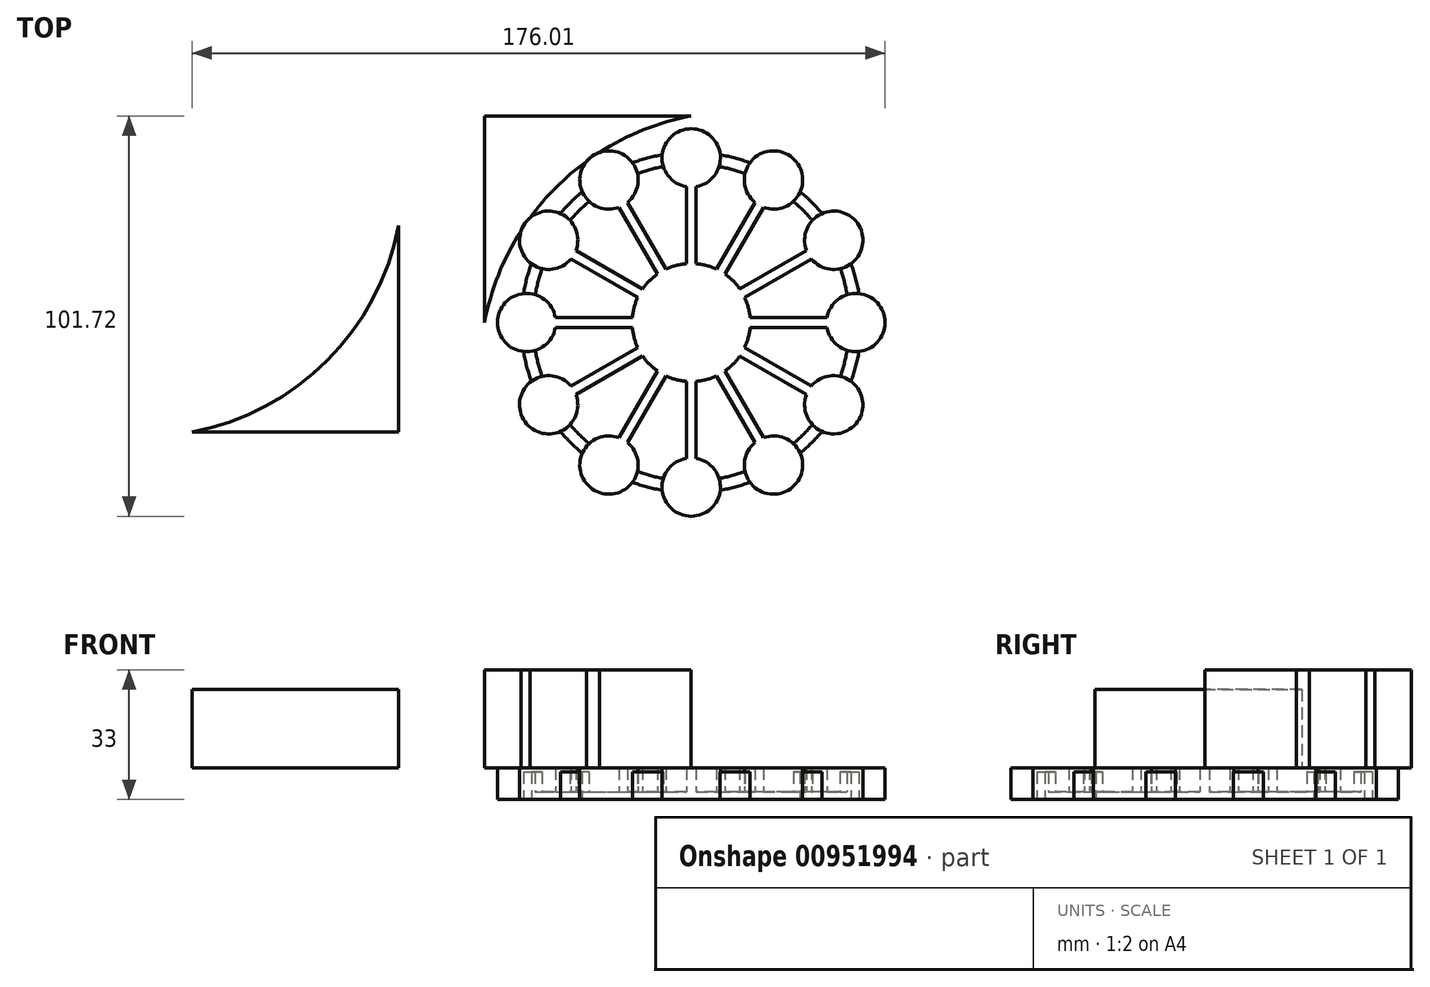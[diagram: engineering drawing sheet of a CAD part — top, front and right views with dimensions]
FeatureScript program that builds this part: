
annotation { "Feature Type Name" : "Feature", "Feature Type Description" : "" }
export const myFeature = defineFeature(function(context is Context, id is Id, definition is map)
    precondition{}
    {
        {
            var Q0;
            Q0=qCreatedBy(makeId("Top.planeOp"),FACE);
            var sketch = newSketch(context, id + "F0", { "sketchPlane" : qUnion([Q0])});
            skCircle(sketch, "E0", {"center": v(0, 0) * mm, "radius": 40.25 * mm});
            skCircle(sketch, "E1", {"center": v(0, 0) * mm, "radius": 43.25 * mm});
            skSolve(sketch);
        }
        {
            var Q0;
            Q0=makeQuery(id+"F0.imprint","IMPRINT",FACE,{"disambiguationData":[TD([[makeQuery(id+"F0.imprint","IMPRINT",EDGE,{"derivedFrom":sQuery(id+"F0.wireOp",EDGE,"E0")}),1.0]])]});
            extrude(context, id + "F1", {"entities" : qUnion([Q0]), "depth" : 2 * mm, "offsetDistance" : 25 * mm});
        }
        {
            var Q0;
            Q0=qSketchRegion(id+"F0",true);
            extrude(context, id + "F2", {"entities" : qUnion([Q0]), "operationType" : NewBodyOperationType.ADD, "depth" : 7 * mm, "offsetDistance" : 25 * mm});
        }
        {
            var Q0;
            Q0=makeQuery(id+"F1.opExtrude","CAP_FACE",FACE,{"disambiguationData":[OSD([sQuery(id+"F0.wireOp",EDGE,"E0")])],"isStart":false});
            var sketch = newSketch(context, id + "F3", { "sketchPlane" : qUnion([Q0])});
            skCircle(sketch, "E2", {"center": v(0, 0) * mm, "radius": 15 * mm});
            skPoint(sketch, "E3.middle", {"position": v(0, 30.91) * mm});
            skCircle(sketch, "E4", {"center": v(0, 0) * mm, "radius": 30.79 * mm, "construction": true});
            skCircle(sketch, "E5", {"center": v(0, 0) * mm, "radius": 49.22 * mm, "construction": true});
            skCircle(sketch, "E6", {"center": v(0, 0) * mm, "radius": 41.81 * mm, "construction": true});
            skCircle(sketch, "E7", {"center": v(0, 41.81) * mm, "radius": 7.4 * mm});
            skLineSegment(sketch, "E8.bottom", {"start": v(-1.25, 14.95) * mm, "end": v(1.25, 14.95) * mm});
            skLineSegment(sketch, "E8.top", {"start": v(-1.25, 35.62) * mm, "end": v(1.25, 35.62) * mm});
            skLineSegment(sketch, "E8.left", {"start": v(-1.25, 14.95) * mm, "end": v(-1.25, 35.62) * mm});
            skLineSegment(sketch, "E8.right", {"start": v(1.25, 14.95) * mm, "end": v(1.25, 35.62) * mm});
            skPoint(sketch, "E8.middle", {"position": v(0, 25.28) * mm});
            skSolve(sketch);
        }
        {
            var Q0;
            Q0 = qSketchRegion(id + "F3", true);
            extrude(context, id + "F4", {"entities" : qUnion([Q0]), "operationType" : NewBodyOperationType.ADD, "depth" : 6 * mm, "offsetDistance" : 25 * mm, "hasSecondDirection" : true, "secondDirectionOppositeDirection" : true, "secondDirectionDepth" : 2 * mm});
        }
        {
            var Q0;
            Q0=makeQuery(id+"F1.opExtrude","SWEPT_BODY",BODY,{"disambiguationData":[OSD([sQuery(id+"F0.wireOp",EDGE,"E0")])]});
            var Q1;
            Q1=makeQuery(id+"F4.opExtrude","CAP_EDGE",EDGE,{"disambiguationData":[OSD([sQuery(id+"F3.wireOp",EDGE,"E2")])],"isStart":false});
            circularPattern(context, id + "F5", {"entities" : qUnion([Q0]), "axis" : qUnion([Q1]), "angle" : 360 * degree, "instanceCount" : 12, "equalSpace" : true});
        }
        {
            var Q0;
            Q0=makeQuery(id+"F1.opExtrude","SWEPT_BODY",BODY,{"disambiguationData":[OSD([sQuery(id+"F0.wireOp",EDGE,"E0")])]});
            var Q1;
            Q1=makeQuery(id+"F5.opPattern","COPY",BODY,{"derivedFrom":makeQuery(id+"F1.opExtrude","SWEPT_BODY",BODY,{"disambiguationData":[OSD([sQuery(id+"F0.wireOp",EDGE,"E0")])]}),"instanceName":"4"});
            var Q2;
            Q2=makeQuery(id+"F5.opPattern","COPY",BODY,{"derivedFrom":makeQuery(id+"F1.opExtrude","SWEPT_BODY",BODY,{"disambiguationData":[OSD([sQuery(id+"F0.wireOp",EDGE,"E0")])]}),"instanceName":"5"});
            var Q3;
            Q3=makeQuery(id+"F5.opPattern","COPY",BODY,{"derivedFrom":makeQuery(id+"F1.opExtrude","SWEPT_BODY",BODY,{"disambiguationData":[OSD([sQuery(id+"F0.wireOp",EDGE,"E0")])]}),"instanceName":"6"});
            var Q4;
            Q4=makeQuery(id+"F5.opPattern","COPY",BODY,{"derivedFrom":makeQuery(id+"F1.opExtrude","SWEPT_BODY",BODY,{"disambiguationData":[OSD([sQuery(id+"F0.wireOp",EDGE,"E0")])]}),"instanceName":"7"});
            var Q5;
            Q5=makeQuery(id+"F5.opPattern","COPY",BODY,{"derivedFrom":makeQuery(id+"F1.opExtrude","SWEPT_BODY",BODY,{"disambiguationData":[OSD([sQuery(id+"F0.wireOp",EDGE,"E0")])]}),"instanceName":"9"});
            var Q6;
            Q6=makeQuery(id+"F5.opPattern","COPY",BODY,{"derivedFrom":makeQuery(id+"F1.opExtrude","SWEPT_BODY",BODY,{"disambiguationData":[OSD([sQuery(id+"F0.wireOp",EDGE,"E0")])]}),"instanceName":"8"});
            var Q7;
            Q7=makeQuery(id+"F5.opPattern","COPY",BODY,{"derivedFrom":makeQuery(id+"F1.opExtrude","SWEPT_BODY",BODY,{"disambiguationData":[OSD([sQuery(id+"F0.wireOp",EDGE,"E0")])]}),"instanceName":"10"});
            var Q8;
            Q8=makeQuery(id+"F5.opPattern","COPY",BODY,{"derivedFrom":makeQuery(id+"F1.opExtrude","SWEPT_BODY",BODY,{"disambiguationData":[OSD([sQuery(id+"F0.wireOp",EDGE,"E0")])]}),"instanceName":"11"});
            var Q9;
            Q9=makeQuery(id+"F5.opPattern","COPY",BODY,{"derivedFrom":makeQuery(id+"F1.opExtrude","SWEPT_BODY",BODY,{"disambiguationData":[OSD([sQuery(id+"F0.wireOp",EDGE,"E0")])]}),"instanceName":"12"});
            var Q10;
            Q10=makeQuery(id+"F5.opPattern","COPY",BODY,{"derivedFrom":makeQuery(id+"F1.opExtrude","SWEPT_BODY",BODY,{"disambiguationData":[OSD([sQuery(id+"F0.wireOp",EDGE,"E0")])]}),"instanceName":"3"});
            var Q11;
            Q11=makeQuery(id+"F5.opPattern","COPY",BODY,{"derivedFrom":makeQuery(id+"F1.opExtrude","SWEPT_BODY",BODY,{"disambiguationData":[OSD([sQuery(id+"F0.wireOp",EDGE,"E0")])]}),"instanceName":"2"});
            var Q12;
            Q12=makeQuery(id+"F5.opPattern","COPY",BODY,{"derivedFrom":makeQuery(id+"F1.opExtrude","SWEPT_BODY",BODY,{"disambiguationData":[OSD([sQuery(id+"F0.wireOp",EDGE,"E0")])]}),"instanceName":"1"});
            var Q13;
            Q13=makeQuery(id+"F5.opPattern","COPY",BODY,{"derivedFrom":makeQuery(id+"F1.opExtrude","SWEPT_BODY",BODY,{"disambiguationData":[OSD([sQuery(id+"F0.wireOp",EDGE,"E0")])]}),"instanceName":"13"});
            booleanBodies(context, id + "F6", {"operationType" : BooleanOperationType.UNION, "tools" : qUnion([Q0, Q1, Q2, Q3, Q4, Q5, Q6, Q7, Q8, Q9, Q10, Q11, Q12, Q13])});
        }
        {
            var Q0;
            {var subQ0=makeQuery(id+"F4.opExtrude","CAP_FACE",FACE,{"disambiguationData":[OSD([sQuery(id+"F3.wireOp",EDGE,"E2"),sQuery(id+"F3.wireOp",EDGE,"E7"),sQuery(id+"F3.wireOp",EDGE,"E8.left"),sQuery(id+"F3.wireOp",EDGE,"E8.right")])],"isStart":false});Q0=makeQuery(id+"F6.opBoolean","MERGE",FACE,{"derivedFrom":[subQ0,makeQuery(id+"F5.opPattern","COPY",FACE,{"derivedFrom":subQ0,"instanceName":"1"}),makeQuery(id+"F5.opPattern","COPY",FACE,{"derivedFrom":subQ0,"instanceName":"2"}),makeQuery(id+"F5.opPattern","COPY",FACE,{"derivedFrom":subQ0,"instanceName":"3"}),makeQuery(id+"F5.opPattern","COPY",FACE,{"derivedFrom":subQ0,"instanceName":"4"}),makeQuery(id+"F5.opPattern","COPY",FACE,{"derivedFrom":subQ0,"instanceName":"5"}),makeQuery(id+"F5.opPattern","COPY",FACE,{"derivedFrom":subQ0,"instanceName":"6"}),makeQuery(id+"F5.opPattern","COPY",FACE,{"derivedFrom":subQ0,"instanceName":"7"}),makeQuery(id+"F5.opPattern","COPY",FACE,{"derivedFrom":subQ0,"instanceName":"8"}),makeQuery(id+"F5.opPattern","COPY",FACE,{"derivedFrom":subQ0,"instanceName":"9"}),makeQuery(id+"F5.opPattern","COPY",FACE,{"derivedFrom":subQ0,"instanceName":"10"}),makeQuery(id+"F5.opPattern","COPY",FACE,{"derivedFrom":subQ0,"instanceName":"11"})]});}
            var sketch = newSketch(context, id + "F7", { "sketchPlane" : qUnion([Q0])});
            skLineSegment(sketch, "E9.bottom", {"start": v(-52.5, 52.5) * mm, "end": v(52.5, 52.5) * mm});
            skLineSegment(sketch, "E9.top", {"start": v(-52.5, -52.5) * mm, "end": v(52.5, -52.5) * mm});
            skLineSegment(sketch, "E9.left", {"start": v(-52.5, 52.5) * mm, "end": v(-52.5, -52.5) * mm});
            skLineSegment(sketch, "E9.right", {"start": v(52.5, 52.5) * mm, "end": v(52.5, -52.5) * mm});
            skPoint(sketch, "E9.middle", {"position": v(0, 0) * mm});
            skArc(sketch, "E10", {"start": v(0, 52.5) * mm, "mid": v(-34.33, 34.33) * mm, "end": v(-52.5, 0) * mm});
            skArc(sketch, "E11", {"start": v(52.5, 0) * mm, "mid": v(34.31, 34.31) * mm, "end": v(0, 52.5) * mm});
            skArc(sketch, "E12", {"start": v(0, -52.5) * mm, "mid": v(34.4, -34.4) * mm, "end": v(52.5, 0) * mm});
            skLineSegment(sketch, "E13.bottom", {"start": v(-126.8, 24.65) * mm, "end": v(-74.3, 24.65) * mm});
            skLineSegment(sketch, "E13.top", {"start": v(-126.8, -27.85) * mm, "end": v(-74.3, -27.85) * mm});
            skLineSegment(sketch, "E13.left", {"start": v(-126.8, 24.65) * mm, "end": v(-126.8, -27.85) * mm});
            skLineSegment(sketch, "E13.right", {"start": v(-74.3, 24.65) * mm, "end": v(-74.3, -27.85) * mm});
            skArc(sketch, "E14", {"start": v(-126.8, -27.85) * mm, "mid": v(-92.46, -9.68) * mm, "end": v(-74.3, 24.65) * mm});
            skSolve(sketch);
        }
        {
            var Q0;
            {var subQ3=sQuery(id+"F7.wireOp",EDGE,"E10");Q0=makeQuery(id+"F7.imprint","IMPRINT",FACE,{"disambiguationData":[TD([[makeQuery(id+"F7.imprint","IMPRINT",EDGE,{"derivedFrom":subQ3}),-1.0]])]});}
            extrude(context, id + "F8", {"entities" : qUnion([Q0]), "depth" : 25 * mm, "offsetDistance" : 25 * mm});
        }
        {
            var Q0;
            Q0=makeQuery(id+"F7.imprint","IMPRINT",FACE,{"disambiguationData":[TD([[makeQuery(id+"F7.imprint","IMPRINT",EDGE,{"derivedFrom":sQuery(id+"F7.wireOp",EDGE,"E13.top")}),1.0]])]});
            extrude(context, id + "F9", {"entities" : qUnion([Q0]), "depth" : 20 * mm, "offsetDistance" : 25 * mm});
        }
    });
